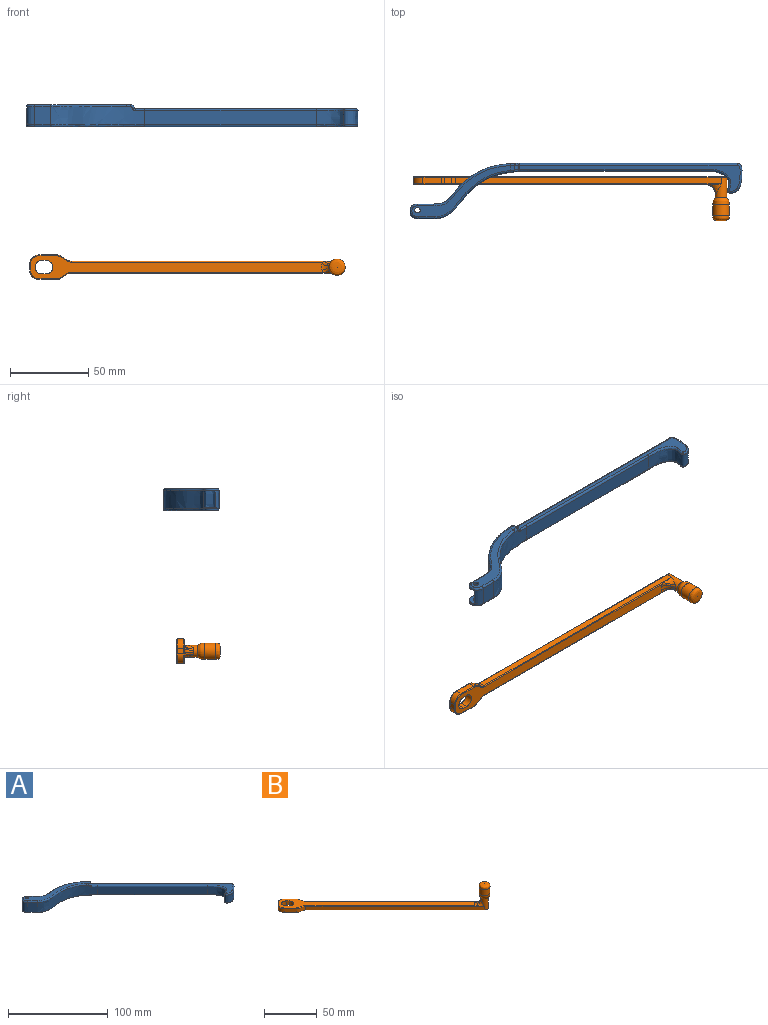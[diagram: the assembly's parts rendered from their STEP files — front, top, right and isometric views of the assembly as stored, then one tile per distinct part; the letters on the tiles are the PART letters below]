
ASSEMBLY  parts=2 mates=2
PART A: 51 faces, bbox 178.5x140.7x14 mm
  f0: extruded ~55.2x18.43mm, area 680.6mm2, adj f2,f6,f9,f16,f17,f18,f25,f46
  f1: extruded ~64.32x21.18mm, area 817mm2, adj f4,f10,f20,f33,f35,f37,f39,f41
  f2: plane 100.37x100.37mm, normal (0.71,0.71,0), area 1321.8mm2, adj f0,f5,f26,f38,f40,f42,f44,f46
  f3: plane 2.09x2.09mm, normal (0.71,-0.71,0), area 0.1mm2, adj f29,f30,f35,f37,f42
  f4: plane 77.69x77.69mm, normal (-0.71,-0.71,0), area 1021.8mm2, adj f1,f5,f22,f31
  f5: extruded ~25.55x20.96mm, area 503mm2, adj f2,f4,f24,f32,f34,f36
  f6: plane 7.35x7.35mm, normal (0.71,0.71,0), area 10.4mm2, adj f0,f7,f18,f23
  f7: extruded ~11.8x9.01mm, area 82.8mm2, adj f6,f9,f10,f14,f17,f18,f21,f47
  f8: cylinder r=1.75mm len=3.5mm, axis (0,0,-1), area 22mm2, adj f13,f18
  f9: plane 7.35x7.35mm, normal (0.71,0.71,0), area 3.1mm2, adj f0,f7,f17,f49
  f10: plane 11.8x6.87mm, normal (-0.71,-0.71,0), area 114.6mm2, adj f1,f7,f19,f45
  f11: cylinder r=1.75mm len=3.5mm, axis (0,0,-1), area 16.5mm2, adj f12,f17
  f12: plane 66.36x27.28mm, normal (0,0,1), area 354.8mm2, adj f11,f28,f43,f45,f47,f48,f49,f50
  f13: plane 169.93x138.3mm, normal (0,0,-1), area 941mm2, adj f8,f19,f20,f21,f22,f23,f24,f25
  f14: extruded ~10.5x3.59mm, area 46.7mm2, adj f7,f15,f17,f18
  f15: plane 10.5x4.24mm, normal (0.71,0.71,0), area 63mm2, adj f14,f16,f17,f18
  f16: extruded ~11.29x10.5mm, area 130.6mm2, adj f0,f15,f17,f18
  f17: plane 17.88x13.38mm, normal (0,0,-1), area 111.2mm2, adj f0,f7,f9,f11,f14,f15,f16
  f18: plane 17.88x13.38mm, normal (0,0,1), area 111.2mm2, adj f0,f6,f7,f8,f14,f15,f16
  f19: cylinder r=1mm len=7.57mm, axis (0.71,-0.71,0), area 15.3mm2, adj f10,f13,f20,f21
  f20: bspline ~88.33x45.2mm, area 111.4mm2, adj f1,f13,f19,f22
  f21: bspline ~10.45x9.62mm, area 23.4mm2, adj f7,f13,f19,f23
  f22: cylinder r=1mm len=78.4mm, axis (0.71,-0.71,0), area 172.6mm2, adj f4,f13,f20,f24
  f23: cylinder r=1mm len=8.06mm, axis (-0.71,0.71,0), area 16.3mm2, adj f6,f13,f21,f25
  f24: bspline ~32.07x26.82mm, area 82.5mm2, adj f5,f13,f22,f26
  f25: bspline ~69.71x32.53mm, area 95.5mm2, adj f0,f13,f23,f26
  f26: cylinder r=1mm len=101.07mm, axis (-0.71,0.71,0), area 222.9mm2, adj f2,f13,f24,f25
  f27: plane 108.98x101.05mm, normal (0,0,1), area 466.2mm2, adj f29,f31,f32,f33,f36,f38
  f28: extruded ~4.27x4.27mm, area 8.4mm2, adj f12,f30,f41,f43,f48
  f29: cylinder r=3mm len=2.51mm, axis (-0.71,-0.71,0), area 1.9mm2, adj f3,f27,f35,f40
  f30: cylinder r=2.3mm len=3.77mm, axis (-0.71,-0.71,0), area 10.8mm2, adj f3,f28,f39,f44,f46
  f31: cylinder r=1.2mm len=78.54mm, axis (-0.71,0.71,0), area 207.1mm2, adj f4,f27,f32,f33
  f32: bspline ~23.8x10.86mm, area 53mm2, adj f5,f27,f31,f34
  f33: bspline ~9.61x9.03mm, area 11.2mm2, adj f1,f27,f31,f35
  f34: bspline ~1.2x1.2mm, area 0.5mm2, adj f5,f32,f36
  f35: bspline ~2.61x2.07mm, area 2.1mm2, adj f1,f3,f29,f33,f37
  f36: bspline ~18.06x16.57mm, area 46mm2, adj f5,f27,f34,f38
  f37: cylinder r=1.2mm len=1.62mm, axis (0,0,-1), area 0.7mm2, adj f1,f3,f35,f39
  f38: cylinder r=1.2mm len=99.37mm, axis (0.71,-0.71,0), area 262.6mm2, adj f2,f27,f36,f40
  f39: bspline ~2.85x2.82mm, area 5.3mm2, adj f1,f30,f37,f41
  f40: torus R=4.2mm, axis (-0.71,-0.71,0), area 2.3mm2, adj f2,f29,f38,f42
  f41: bspline ~3.94x3.39mm, area 5.1mm2, adj f1,f28,f39,f43
  f42: cylinder r=1.2mm len=1.7mm, axis (0,0,-1), area 0.7mm2, adj f2,f3,f40,f44
  f43: bspline ~72.6x30.41mm, area 111.8mm2, adj f1,f12,f28,f41,f45
  f44: torus R=1.1mm, axis (-0.71,-0.71,0), area 4.3mm2, adj f2,f30,f42,f46
  f45: cylinder r=1.2mm len=7.71mm, axis (-0.71,0.71,0), area 18.3mm2, adj f10,f12,f43,f47
  f46: bspline ~1.96x1.95mm, area 1.3mm2, adj f0,f2,f30,f44,f48
  f47: bspline ~12.2x10.08mm, area 27.7mm2, adj f7,f12,f45,f49
  f48: bspline ~3.75x3.68mm, area 5.2mm2, adj f0,f12,f28,f46,f50
  f49: cylinder r=1.2mm len=8.2mm, axis (0.71,-0.71,0), area 19.6mm2, adj f9,f12,f47,f50
  f50: bspline ~60.16x23.6mm, area 108.4mm2, adj f0,f12,f48,f49
PART B: 55 faces, bbox 147.8x147.8x28.1 mm
  f0: torus R=9.75mm, axis (0,0,1), area 18.1mm2, adj f11,f21,f53,f54
  f1: bspline ~6.26x6.17mm, area 13.3mm2, adj f11,f26,f54
  f2: bspline ~6.26x6.17mm, area 13.3mm2, adj f11,f38,f53
  f3: cylinder r=6mm len=8.49mm, axis (0,0,-1), area 37.7mm2, adj f4,f20,f33,f52
  f4: plane 4x2.55mm, normal (-0.71,0.71,0), area 14.4mm2, adj f3,f5,f32,f51
  f5: cylinder r=6mm len=8.49mm, axis (0,0,-1), area 37.7mm2, adj f4,f6,f31,f49
  f6: plane 8.2x8.2mm, normal (-0.71,-0.71,0), area 46.4mm2, adj f5,f7,f30,f47
  f7: cylinder r=4.2mm len=4mm, axis (0,0,-1), area 9.1mm2, adj f6,f8,f29,f45
  f8: plane 5.4x4mm, normal (-0.24,-0.97,0), area 22.3mm2, adj f7,f9,f28,f43
  f9: cylinder r=4mm len=4mm, axis (0,0,-1), area 8.7mm2, adj f8,f10,f27,f41
  f10: plane 120.21x120.21mm, normal (-0.71,-0.71,0), area 680mm2, adj f9,f11,f26,f39
  f11: cylinder r=3.75mm len=12.5mm, axis (0,0,-1), area 193.5mm2, adj f0,f1,f2,f10,f12,f24,f40,f53
  f12: plane 120.21x120.21mm, normal (0.71,0.71,0), area 680mm2, adj f11,f13,f38,f42
  f13: cylinder r=4mm len=4mm, axis (0,0,-1), area 8.7mm2, adj f12,f14,f37,f44
  f14: plane 5.4x4mm, normal (0.97,0.24,0), area 22.3mm2, adj f13,f15,f36,f46
  f15: cylinder r=4.2mm len=4mm, axis (0,0,-1), area 9.1mm2, adj f14,f20,f35,f48
  f16: cylinder r=4.3mm len=7.34mm, axis (0,0,-1), area 67.5mm2, adj f17,f19,f21,f22
  f17: plane 5x1.98mm, normal (-0.71,-0.71,0), area 14mm2, adj f16,f18,f21,f22
  f18: cylinder r=4.3mm len=7.34mm, axis (0,0,-1), area 67.5mm2, adj f17,f19,f21,f22
  f19: plane 5x1.98mm, normal (0.71,0.71,0), area 14mm2, adj f16,f18,f21,f22
  f20: plane 8.2x8.2mm, normal (0.71,0.71,0), area 46.4mm2, adj f3,f15,f34,f50
  f21: plane 137.41x137.41mm, normal (0,0,1), area 1291.5mm2, adj f0,f16,f17,f18,f19,f26,f27,f28
  f22: plane 144.8x144.8mm, normal (0,0,-1), area 1370.2mm2, adj f16,f17,f18,f19,f39,f40,f41,f42
  f23: cylinder r=5.2mm len=10.4mm, axis (0,0,-1), area 228.7mm2, adj f24,f25
  f24: revolved ~10.39x10.39mm, area 159.4mm2, adj f11,f23
  f25: revolved ~10.4x10.4mm, area 150.4mm2, adj f23
  f26: cylinder r=0.5mm len=120.56mm, axis (-0.71,0.71,0), area 129.5mm2, adj f1,f10,f21,f27,f54
  f27: torus R=4.5mm, axis (0,0,1), area 1.8mm2, adj f9,f21,f26,f28
  f28: cylinder r=0.5mm len=5.52mm, axis (-0.97,0.24,0), area 4.4mm2, adj f8,f21,f27,f29
  f29: torus R=3.7mm, axis (0,0,1), area 1.7mm2, adj f7,f21,f28,f30
  f30: cylinder r=0.5mm len=8.56mm, axis (-0.71,0.71,0), area 9.1mm2, adj f6,f21,f29,f31
  f31: torus R=5.5mm, axis (0,0,1), area 7.2mm2, adj f5,f21,f30,f32
  f32: cylinder r=0.5mm len=2.9mm, axis (0.71,0.71,0), area 2.8mm2, adj f4,f21,f31,f33
  f33: torus R=5.5mm, axis (0,0,1), area 7.2mm2, adj f3,f21,f32,f34
  f34: cylinder r=0.5mm len=8.56mm, axis (0.71,-0.71,0), area 9.1mm2, adj f20,f21,f33,f35
  f35: torus R=3.7mm, axis (0,0,1), area 1.7mm2, adj f15,f21,f34,f36
  f36: cylinder r=0.5mm len=5.52mm, axis (0.24,-0.97,0), area 4.4mm2, adj f14,f21,f35,f37
  f37: torus R=4.5mm, axis (0,0,1), area 1.8mm2, adj f13,f21,f36,f38
  f38: cylinder r=0.5mm len=120.56mm, axis (0.71,-0.71,0), area 129.5mm2, adj f2,f12,f21,f37,f53
  f39: cylinder r=0.5mm len=120.56mm, axis (0.71,-0.71,0), area 133.5mm2, adj f10,f22,f40,f41
  f40: torus R=3.25mm, axis (0,0,1), area 8.8mm2, adj f11,f22,f39,f42
  f41: torus R=4.5mm, axis (0,0,1), area 1.8mm2, adj f9,f22,f39,f43
  f42: cylinder r=0.5mm len=120.56mm, axis (-0.71,0.71,0), area 133.5mm2, adj f12,f22,f40,f44
  f43: cylinder r=0.5mm len=5.52mm, axis (0.97,-0.24,0), area 4.4mm2, adj f8,f22,f41,f45
  f44: torus R=4.5mm, axis (0,0,1), area 1.8mm2, adj f13,f22,f42,f46
  f45: torus R=3.7mm, axis (0,0,1), area 1.7mm2, adj f7,f22,f43,f47
  f46: cylinder r=0.5mm len=5.52mm, axis (-0.24,0.97,0), area 4.4mm2, adj f14,f22,f44,f48
  f47: cylinder r=0.5mm len=8.56mm, axis (0.71,-0.71,0), area 9.1mm2, adj f6,f22,f45,f49
  f48: torus R=3.7mm, axis (0,0,1), area 1.7mm2, adj f15,f22,f46,f50
  f49: torus R=5.5mm, axis (0,0,1), area 7.2mm2, adj f5,f22,f47,f51
  f50: cylinder r=0.5mm len=8.56mm, axis (-0.71,0.71,0), area 9.1mm2, adj f20,f22,f48,f52
  f51: cylinder r=0.5mm len=2.9mm, axis (-0.71,-0.71,0), area 2.8mm2, adj f4,f22,f49,f52
  f52: torus R=5.5mm, axis (0,0,1), area 7.2mm2, adj f3,f22,f50,f51
  f53: bspline ~6.36x5.81mm, area 15.9mm2, adj f0,f2,f11,f21,f38
  f54: bspline ~6.37x5.81mm, area 15.9mm2, adj f0,f1,f11,f21,f26
PLACE A rot(axis=(0,0,1),45deg) t=(-55.62,-4.88,16)mm
PLACE B rot(axis=(0.86,-0.36,0.36),98.4deg) t=(-31.5,16.67,-73.94)mm
MATE parallel A.f13 <-> B.f20  axis (0,0,-1) through (-45.22,-1.88,16)mm
MATE parallel A.f2 <-> B.f22  axis (0,1,0) through (77.71,25.12,21.66)mm
